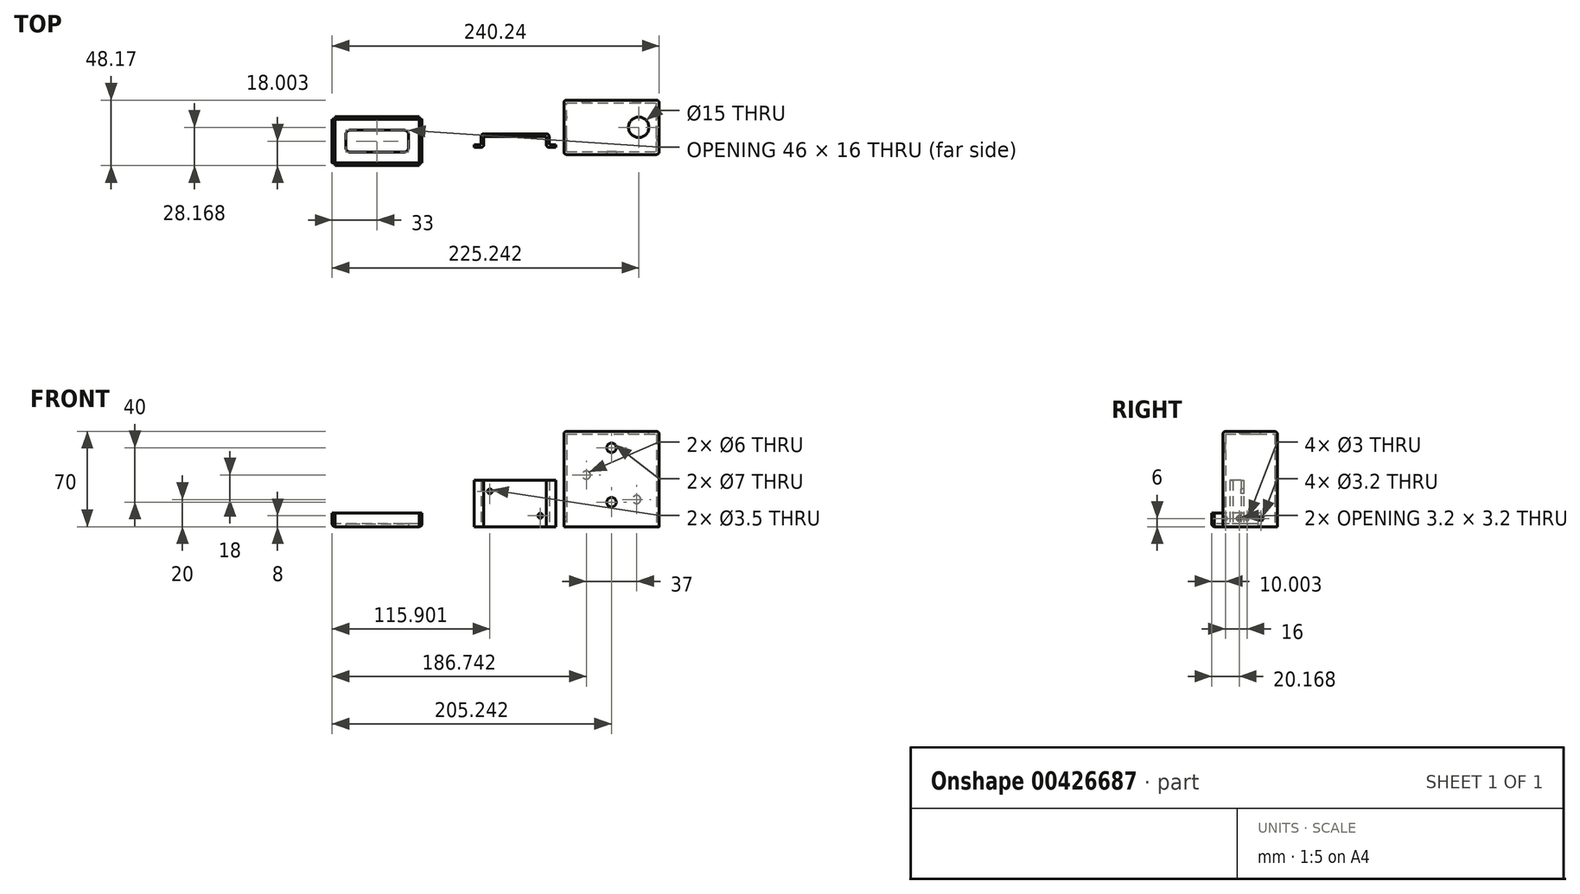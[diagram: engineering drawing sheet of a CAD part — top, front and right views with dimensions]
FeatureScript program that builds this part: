
annotation { "Feature Type Name" : "Feature", "Feature Type Description" : "" }
export const myFeature = defineFeature(function(context is Context, id is Id, definition is map)
    precondition{}
    {
        {
            var Q0;
            Q0=qCreatedBy(makeId("Top.planeOp"),FACE);
            var sketch = newSketch(context, id + "F0", { "sketchPlane" : qUnion([Q0])});
            skLineSegment(sketch, "E0", {"start": v(-40.1, 0) * mm, "end": v(-35.1, 0) * mm});
            skLineSegment(sketch, "E1", {"start": v(-40.1, 0) * mm, "end": v(-40.1, -2) * mm});
            skLineSegment(sketch, "E2", {"start": v(-35.1, 0) * mm, "end": v(-35.1, 6) * mm});
            skLineSegment(sketch, "E3", {"start": v(-33.1, 8) * mm, "end": v(12.9, 8) * mm});
            skLineSegment(sketch, "E4", {"start": v(14.9, 6) * mm, "end": v(14.9, 0) * mm});
            skLineSegment(sketch, "E5", {"start": v(14.9, 0) * mm, "end": v(19.9, 0) * mm});
            skLineSegment(sketch, "E6", {"start": v(19.9, 0) * mm, "end": v(19.9, -2) * mm});
            skLineSegment(sketch, "E7", {"start": v(19.9, -2) * mm, "end": v(14.9, -2) * mm});
            skLineSegment(sketch, "E8", {"start": v(12.9, 0) * mm, "end": v(12.9, 6) * mm});
            skLineSegment(sketch, "E9", {"start": v(12.9, 6) * mm, "end": v(-33.1, 6) * mm});
            skLineSegment(sketch, "E10", {"start": v(-33.1, 6) * mm, "end": v(-33.1, 0) * mm});
            skLineSegment(sketch, "E11", {"start": v(-35.1, -2) * mm, "end": v(-40.1, -2) * mm});
            skPoint(sketch, "E12.visualSharp", {"position": v(-35.1, 8) * mm});
            skArc(sketch, "E12.filletArc", {"start": v(-33.1, 8) * mm, "mid": v(-34.52, 7.41) * mm, "end": v(-35.1, 6) * mm});
            skPoint(sketch, "E13.visualSharp", {"position": v(-33.1, -2) * mm});
            skArc(sketch, "E13.filletArc", {"start": v(-35.1, -2) * mm, "mid": v(-33.7, -1.41) * mm, "end": v(-33.1, 0) * mm});
            skPoint(sketch, "E14.visualSharp", {"position": v(14.9, 8) * mm});
            skArc(sketch, "E14.filletArc", {"start": v(14.9, 6) * mm, "mid": v(14.3, 7.41) * mm, "end": v(12.9, 8) * mm});
            skPoint(sketch, "E15.visualSharp", {"position": v(12.9, -2) * mm});
            skArc(sketch, "E15.filletArc", {"start": v(12.9, 0) * mm, "mid": v(13.48, -1.41) * mm, "end": v(14.9, -2) * mm});
            skSolve(sketch);
        }
        {
            var Q0;
            Q0 = qSketchRegion(id + "F0", true);
            extrude(context, id + "F1", {"entities" : qUnion([Q0]), "depth" : 34 * mm});
        }
        {
            var Q0;
            Q0=makeQuery(id+"F1.opExtrude","SWEPT_FACE",FACE,{"disambiguationData":[OSD([sQuery(id+"F0.wireOp",EDGE,"E9")])]});
            var sketch = newSketch(context, id + "F2", { "sketchPlane" : qUnion([Q0])});
            skPoint(sketch, "E16", {"position": v(-28.6, 26) * mm});
            skPoint(sketch, "E17", {"position": v(8.4, 8) * mm});
            skSolve(sketch);
        }
        {
            var Q0;
            Q0=sQuery(id+"F2.wireOp",VERTEX,"E16");
            var Q1;
            Q1=sQuery(id+"F2.wireOp",VERTEX,"E17");
            var Q2;
            Q2=makeQuery(id+"F1.opExtrude","SWEPT_BODY",BODY,{"disambiguationData":[OSD([sQuery(id+"F0.wireOp",EDGE,"E0"),sQuery(id+"F0.wireOp",EDGE,"E1"),sQuery(id+"F0.wireOp",EDGE,"E2"),sQuery(id+"F0.wireOp",EDGE,"E3"),sQuery(id+"F0.wireOp",EDGE,"E4"),sQuery(id+"F0.wireOp",EDGE,"E5"),sQuery(id+"F0.wireOp",EDGE,"E6"),sQuery(id+"F0.wireOp",EDGE,"E7"),sQuery(id+"F0.wireOp",EDGE,"E8"),sQuery(id+"F0.wireOp",EDGE,"E9"),sQuery(id+"F0.wireOp",EDGE,"E10"),sQuery(id+"F0.wireOp",EDGE,"E11"),sQuery(id+"F0.wireOp",EDGE,"E12.filletArc"),sQuery(id+"F0.wireOp",EDGE,"E13.filletArc"),sQuery(id+"F0.wireOp",EDGE,"E14.filletArc"),sQuery(id+"F0.wireOp",EDGE,"E15.filletArc")])]});
            hole(context, id + "F3", {"style" : HoleStyle.SIMPLE, "endStyle" : HoleEndStyle.THROUGH, "holeDiameter" : 3.5 * mm, "tappedDepth" : 12 * mm, "tapClearance" : 3, "locations" : qUnion([Q0, Q1]), "scope" : qUnion([Q2])});
        }
        {
            var Q0;
            Q0=qCreatedBy(makeId("Top.planeOp"),FACE);
            var sketch = newSketch(context, id + "F4", { "sketchPlane" : qUnion([Q0])});
            skLineSegment(sketch, "E18.bottom", {"start": v(25.73, 32.75) * mm, "end": v(95.73, 32.75) * mm});
            skLineSegment(sketch, "E18.top", {"start": v(25.73, -7.25) * mm, "end": v(95.73, -7.25) * mm});
            skLineSegment(sketch, "E18.left", {"start": v(25.73, 32.75) * mm, "end": v(25.73, -7.25) * mm});
            skLineSegment(sketch, "E18.right", {"start": v(95.73, 32.75) * mm, "end": v(95.73, -7.25) * mm});
            skSolve(sketch);
        }
        {
            var Q0;
            Q0=makeQuery(id+"F4.imprint","IMPRINT",FACE,{"disambiguationData":[TD([[makeQuery(id+"F4.imprint","IMPRINT",EDGE,{"derivedFrom":sQuery(id+"F4.wireOp",EDGE,"E18.bottom")}),-1.0]])]});
            extrude(context, id + "F5", {"entities" : qUnion([Q0]), "depth" : 70 * mm});
        }
        {
            var Q0;
            Q0=makeQuery(id+"F5.opExtrude","CAP_FACE",FACE,{"disambiguationData":[OSD([sQuery(id+"F4.wireOp",EDGE,"E18.bottom"),sQuery(id+"F4.wireOp",EDGE,"E18.top"),sQuery(id+"F4.wireOp",EDGE,"E18.left"),sQuery(id+"F4.wireOp",EDGE,"E18.right")])],"isStart":true});
            var sketch = newSketch(context, id + "F6", { "sketchPlane" : qUnion([Q0])});
            skLineSegment(sketch, "E19.bottom", {"start": v(27.73, 5.25) * mm, "end": v(93.73, 5.25) * mm});
            skLineSegment(sketch, "E19.top", {"start": v(27.73, -30.75) * mm, "end": v(93.73, -30.75) * mm});
            skLineSegment(sketch, "E19.left", {"start": v(27.73, 5.25) * mm, "end": v(27.73, -30.75) * mm});
            skLineSegment(sketch, "E19.right", {"start": v(93.73, 5.25) * mm, "end": v(93.73, -30.75) * mm});
            skSolve(sketch);
        }
        {
            var Q0;
            Q0 = qSketchRegion(id + "F6", true);
            extrude(context, id + "F7", {"entities" : qUnion([Q0]), "operationType" : NewBodyOperationType.REMOVE, "oppositeDirection" : true, "depth" : 68 * mm});
        }
        {
            var Q0;
            Q0=makeQuery(id+"F5.opExtrude","CAP_FACE",FACE,{"disambiguationData":[OSD([sQuery(id+"F4.wireOp",EDGE,"E18.bottom"),sQuery(id+"F4.wireOp",EDGE,"E18.top"),sQuery(id+"F4.wireOp",EDGE,"E18.left"),sQuery(id+"F4.wireOp",EDGE,"E18.right")])],"isStart":false});
            var sketch = newSketch(context, id + "F8", { "sketchPlane" : qUnion([Q0])});
            skPoint(sketch, "E20", {"position": v(80.73, 12.75) * mm});
            skSolve(sketch);
        }
        {
            var Q0;
            Q0=sQuery(id+"F8.wireOp",VERTEX,"E20");
            var Q1;
            Q1=makeQuery(id+"F5.opExtrude","SWEPT_BODY",BODY,{"disambiguationData":[OSD([sQuery(id+"F4.wireOp",EDGE,"E18.bottom"),sQuery(id+"F4.wireOp",EDGE,"E18.top"),sQuery(id+"F4.wireOp",EDGE,"E18.left"),sQuery(id+"F4.wireOp",EDGE,"E18.right")])]});
            hole(context, id + "F9", {"style" : HoleStyle.SIMPLE, "endStyle" : HoleEndStyle.THROUGH, "holeDiameter" : 15 * mm, "tappedDepth" : 12 * mm, "tapClearance" : 3, "locations" : qUnion([Q0]), "scope" : qUnion([Q1])});
        }
        {
            var Q0;
            Q0=makeQuery(id+"F5.opExtrude","SWEPT_FACE",FACE,{"disambiguationData":[OSD([sQuery(id+"F4.wireOp",EDGE,"E18.right")])]});
            var sketch = newSketch(context, id + "F10", { "sketchPlane" : qUnion([Q0])});
            skPoint(sketch, "E21", {"position": v(4.75, 6) * mm});
            skPoint(sketch, "E22", {"position": v(20.75, 6) * mm});
            skSolve(sketch);
        }
        {
            var Q0;
            Q0=sQuery(id+"F10.wireOp",VERTEX,"E22");
            var Q1;
            Q1=sQuery(id+"F10.wireOp",VERTEX,"E21");
            var Q2;
            Q2=makeQuery(id+"F5.opExtrude","SWEPT_BODY",BODY,{"disambiguationData":[OSD([sQuery(id+"F4.wireOp",EDGE,"E18.bottom"),sQuery(id+"F4.wireOp",EDGE,"E18.top"),sQuery(id+"F4.wireOp",EDGE,"E18.left"),sQuery(id+"F4.wireOp",EDGE,"E18.right")])]});
            hole(context, id + "F11", {"style" : HoleStyle.SIMPLE, "endStyle" : HoleEndStyle.THROUGH, "holeDiameter" : 3.2 * mm, "tappedDepth" : 12 * mm, "tapClearance" : 3, "locations" : qUnion([Q0, Q1]), "scope" : qUnion([Q2])});
        }
        {
            var Q0;
            Q0=makeQuery(id+"F5.opExtrude","SWEPT_FACE",FACE,{"disambiguationData":[OSD([sQuery(id+"F4.wireOp",EDGE,"E18.bottom")])]});
            var sketch = newSketch(context, id + "F12", { "sketchPlane" : qUnion([Q0])});
            skCircle(sketch, "E23", {"center": v(-42.23, 38) * mm, "radius": 3 * mm});
            skCircle(sketch, "E24", {"center": v(-79.23, 20) * mm, "radius": 3 * mm});
            skSolve(sketch);
        }
        {
            var Q0;
            Q0=makeQuery(id+"F12.imprint","IMPRINT",FACE,{"disambiguationData":[TD([[makeQuery(id+"F12.imprint","IMPRINT",EDGE,{"derivedFrom":sQuery(id+"F12.wireOp",EDGE,"E23")}),1.0]])]});
            var Q1;
            Q1=makeQuery(id+"F12.imprint","IMPRINT",FACE,{"disambiguationData":[TD([[makeQuery(id+"F12.imprint","IMPRINT",EDGE,{"derivedFrom":sQuery(id+"F12.wireOp",EDGE,"E24")}),1.0]])]});
            extrude(context, id + "F13", {"entities" : qUnion([Q0, Q1]), "operationType" : NewBodyOperationType.REMOVE, "oppositeDirection" : true, "depth" : 2 * mm});
        }
        {
            var Q0;
            Q0=qCreatedBy(makeId("Top.planeOp"),FACE);
            var sketch = newSketch(context, id + "F14", { "sketchPlane" : qUnion([Q0])});
            skLineSegment(sketch, "E25.bottom", {"start": v(-142.5, 20.58) * mm, "end": v(-80.5, 20.58) * mm});
            skLineSegment(sketch, "E25.top", {"start": v(-142.5, -15.42) * mm, "end": v(-80.5, -15.42) * mm});
            skLineSegment(sketch, "E25.left", {"start": v(-144.5, 18.58) * mm, "end": v(-144.5, -13.42) * mm});
            skLineSegment(sketch, "E25.right", {"start": v(-78.5, 18.58) * mm, "end": v(-78.5, -13.42) * mm});
            skLineSegment(sketch, "E26", {"start": v(-142.5, 20.58) * mm, "end": v(-142.5, -15.42) * mm});
            skLineSegment(sketch, "E27", {"start": v(-144.5, 18.58) * mm, "end": v(-78.5, 18.58) * mm});
            skLineSegment(sketch, "E28", {"start": v(-80.5, 20.58) * mm, "end": v(-80.5, -15.42) * mm});
            skLineSegment(sketch, "E29", {"start": v(-144.5, -13.42) * mm, "end": v(-78.5, -13.42) * mm});
            skLineSegment(sketch, "E30.bottom", {"start": v(-131.5, 10.58) * mm, "end": v(-91.5, 10.58) * mm});
            skLineSegment(sketch, "E30.top", {"start": v(-131.5, -5.42) * mm, "end": v(-91.5, -5.42) * mm});
            skLineSegment(sketch, "E30.left", {"start": v(-134.5, 7.58) * mm, "end": v(-134.5, -2.42) * mm});
            skLineSegment(sketch, "E30.right", {"start": v(-88.5, 7.58) * mm, "end": v(-88.5, -2.42) * mm});
            skPoint(sketch, "E31.visualSharp", {"position": v(-134.5, 10.58) * mm});
            skArc(sketch, "E31.filletArc", {"start": v(-131.5, 10.58) * mm, "mid": v(-133.63, 9.7) * mm, "end": v(-134.5, 7.58) * mm});
            skPoint(sketch, "E32.visualSharp", {"position": v(-134.5, -5.42) * mm});
            skArc(sketch, "E32.filletArc", {"start": v(-134.5, -2.42) * mm, "mid": v(-133.63, -4.54) * mm, "end": v(-131.5, -5.42) * mm});
            skPoint(sketch, "E33.visualSharp", {"position": v(-88.5, -5.42) * mm});
            skArc(sketch, "E33.filletArc", {"start": v(-91.5, -5.42) * mm, "mid": v(-89.39, -4.54) * mm, "end": v(-88.5, -2.42) * mm});
            skPoint(sketch, "E34.visualSharp", {"position": v(-88.5, 10.58) * mm});
            skArc(sketch, "E34.filletArc", {"start": v(-88.5, 7.58) * mm, "mid": v(-89.39, 9.7) * mm, "end": v(-91.5, 10.58) * mm});
            skSolve(sketch);
        }
        {
            var Q0;
            Q0=makeQuery(id+"F14.imprint","IMPRINT",FACE,{"disambiguationData":[TD([[makeQuery(id+"F14.imprint","IMPRINT",EDGE,{"derivedFrom":sQuery(id+"F14.wireOp",EDGE,"E30.bottom")}),1.0]])]});
            var Q1;
            {var subQ0=sQuery(id+"F14.wireOp",EDGE,"E25.right");Q1=makeQuery(id+"F14.imprint","IMPRINT",FACE,{"disambiguationData":[TD([[makeQuery(id+"F14.imprint","IMPRINT",EDGE,{"derivedFrom":subQ0}),-1.0]])]});}
            var Q2;
            {var subQ0=sQuery(id+"F14.wireOp",EDGE,"E25.top");Q2=makeQuery(id+"F14.imprint","IMPRINT",FACE,{"disambiguationData":[TD([[makeQuery(id+"F14.imprint","IMPRINT",EDGE,{"derivedFrom":subQ0}),1.0]])]});}
            var Q3;
            {var subQ0=sQuery(id+"F14.wireOp",EDGE,"E25.left");Q3=makeQuery(id+"F14.imprint","IMPRINT",FACE,{"disambiguationData":[TD([[makeQuery(id+"F14.imprint","IMPRINT",EDGE,{"derivedFrom":subQ0}),1.0]])]});}
            var Q4;
            {var subQ0=sQuery(id+"F14.wireOp",EDGE,"E25.bottom");Q4=makeQuery(id+"F14.imprint","IMPRINT",FACE,{"disambiguationData":[TD([[makeQuery(id+"F14.imprint","IMPRINT",EDGE,{"derivedFrom":subQ0}),-1.0]])]});}
            extrude(context, id + "F15", {"entities" : qUnion([Q0, Q1, Q2, Q3, Q4]), "depth" : 2 * mm});
        }
        {
            var Q0;
            Q0=makeQuery(id+"F15.opExtrude","CAP_FACE",FACE,{"disambiguationData":[OSD([sQuery(id+"F14.wireOp",EDGE,"E25.bottom"),sQuery(id+"F14.wireOp",EDGE,"E25.top"),sQuery(id+"F14.wireOp",EDGE,"E25.left"),sQuery(id+"F14.wireOp",EDGE,"E25.right"),sQuery(id+"F14.wireOp",EDGE,"E26"),sQuery(id+"F14.wireOp",EDGE,"E27"),sQuery(id+"F14.wireOp",EDGE,"E28"),sQuery(id+"F14.wireOp",EDGE,"E29"),sQuery(id+"F14.wireOp",EDGE,"E30.bottom"),sQuery(id+"F14.wireOp",EDGE,"E30.top"),sQuery(id+"F14.wireOp",EDGE,"E30.left"),sQuery(id+"F14.wireOp",EDGE,"E30.right"),sQuery(id+"F14.wireOp",EDGE,"E31.filletArc"),sQuery(id+"F14.wireOp",EDGE,"E32.filletArc"),sQuery(id+"F14.wireOp",EDGE,"E33.filletArc"),sQuery(id+"F14.wireOp",EDGE,"E34.filletArc")])],"isStart":false});
            var sketch = newSketch(context, id + "F16", { "sketchPlane" : qUnion([Q0])});
            skLineSegment(sketch, "E35.bottom", {"start": v(-144.5, 18.58) * mm, "end": v(-142.6, 18.58) * mm});
            skLineSegment(sketch, "E35.top", {"start": v(-144.5, -13.42) * mm, "end": v(-142.6, -13.42) * mm});
            skLineSegment(sketch, "E35.left", {"start": v(-144.5, 18.58) * mm, "end": v(-144.5, -13.42) * mm});
            skLineSegment(sketch, "E35.right", {"start": v(-142.5, 18.48) * mm, "end": v(-142.5, -13.32) * mm});
            skLineSegment(sketch, "E36.bottom", {"start": v(-142.4, 18.58) * mm, "end": v(-80.6, 18.58) * mm});
            skLineSegment(sketch, "E36.top", {"start": v(-142.5, 20.58) * mm, "end": v(-80.5, 20.58) * mm});
            skLineSegment(sketch, "E36.left", {"start": v(-142.5, 18.68) * mm, "end": v(-142.5, 20.58) * mm});
            skLineSegment(sketch, "E36.right", {"start": v(-80.5, 18.68) * mm, "end": v(-80.5, 20.58) * mm});
            skLineSegment(sketch, "E37.bottom", {"start": v(-80.4, 18.58) * mm, "end": v(-78.5, 18.58) * mm});
            skLineSegment(sketch, "E37.top", {"start": v(-80.4, -13.42) * mm, "end": v(-78.5, -13.42) * mm});
            skLineSegment(sketch, "E37.left", {"start": v(-80.5, 18.48) * mm, "end": v(-80.5, -13.32) * mm});
            skLineSegment(sketch, "E37.right", {"start": v(-78.5, 18.58) * mm, "end": v(-78.5, -13.42) * mm});
            skLineSegment(sketch, "E38.bottom", {"start": v(-80.6, -13.42) * mm, "end": v(-142.4, -13.42) * mm});
            skLineSegment(sketch, "E38.top", {"start": v(-80.5, -15.42) * mm, "end": v(-142.5, -15.42) * mm});
            skLineSegment(sketch, "E38.left", {"start": v(-80.5, -13.52) * mm, "end": v(-80.5, -15.42) * mm});
            skLineSegment(sketch, "E38.right", {"start": v(-142.5, -13.52) * mm, "end": v(-142.5, -15.42) * mm});
            skPoint(sketch, "E39.visualSharp", {"position": v(-142.5, 18.58) * mm});
            skArc(sketch, "E39.filletArc", {"start": v(-142.5, 18.48) * mm, "mid": v(-142.54, 18.55) * mm, "end": v(-142.6, 18.58) * mm});
            skArc(sketch, "E40.filletArc", {"start": v(-142.5, 18.68) * mm, "mid": v(-142.48, 18.61) * mm, "end": v(-142.4, 18.58) * mm});
            skPoint(sketch, "E41.visualSharp", {"position": v(-80.5, 18.58) * mm});
            skArc(sketch, "E41.filletArc", {"start": v(-80.6, 18.58) * mm, "mid": v(-80.54, 18.61) * mm, "end": v(-80.5, 18.68) * mm});
            skArc(sketch, "E42.filletArc", {"start": v(-80.4, 18.58) * mm, "mid": v(-80.48, 18.55) * mm, "end": v(-80.5, 18.48) * mm});
            skPoint(sketch, "E43.visualSharp", {"position": v(-80.5, -13.42) * mm});
            skArc(sketch, "E43.filletArc", {"start": v(-80.5, -13.32) * mm, "mid": v(-80.48, -13.39) * mm, "end": v(-80.4, -13.42) * mm});
            skArc(sketch, "E44.filletArc", {"start": v(-80.5, -13.52) * mm, "mid": v(-80.54, -13.45) * mm, "end": v(-80.6, -13.42) * mm});
            skPoint(sketch, "E45.visualSharp", {"position": v(-142.5, -13.42) * mm});
            skArc(sketch, "E45.filletArc", {"start": v(-142.4, -13.42) * mm, "mid": v(-142.48, -13.45) * mm, "end": v(-142.5, -13.52) * mm});
            skArc(sketch, "E46.filletArc", {"start": v(-142.6, -13.42) * mm, "mid": v(-142.54, -13.39) * mm, "end": v(-142.5, -13.32) * mm});
            skSolve(sketch);
        }
        {
            var Q0;
            Q0=makeQuery(id+"F16.imprint","IMPRINT",FACE,{"disambiguationData":[TD([[makeQuery(id+"F16.imprint","IMPRINT",EDGE,{"derivedFrom":sQuery(id+"F16.wireOp",EDGE,"E36.bottom")}),1.0]])]});
            var Q1;
            Q1=makeQuery(id+"F16.imprint","IMPRINT",FACE,{"disambiguationData":[TD([[makeQuery(id+"F16.imprint","IMPRINT",EDGE,{"derivedFrom":sQuery(id+"F16.wireOp",EDGE,"E35.bottom")}),-1.0]])]});
            var Q2;
            Q2=makeQuery(id+"F16.imprint","IMPRINT",FACE,{"disambiguationData":[TD([[makeQuery(id+"F16.imprint","IMPRINT",EDGE,{"derivedFrom":sQuery(id+"F16.wireOp",EDGE,"E38.bottom")}),1.0]])]});
            var Q3;
            Q3=makeQuery(id+"F16.imprint","IMPRINT",FACE,{"disambiguationData":[TD([[makeQuery(id+"F16.imprint","IMPRINT",EDGE,{"derivedFrom":sQuery(id+"F16.wireOp",EDGE,"E37.bottom")}),-1.0]])]});
            extrude(context, id + "F17", {"entities" : qUnion([Q0, Q1, Q2, Q3]), "operationType" : NewBodyOperationType.ADD, "depth" : 8 * mm});
        }
        {
            var Q0;
            Q0=makeQuery(id+"F17.boolean.opBoolean","MERGE",FACE,{"derivedFrom":[makeQuery(id+"F15.opExtrude","SWEPT_FACE",FACE,{"disambiguationData":[OSD([sQuery(id+"F14.wireOp",EDGE,"E25.left")])]}),makeQuery(id+"F17.opExtrude","SWEPT_FACE",FACE,{"disambiguationData":[OSD([sQuery(id+"F16.wireOp",EDGE,"E35.left")])]})]});
            var sketch = newSketch(context, id + "F18", { "sketchPlane" : qUnion([Q0])});
            skPoint(sketch, "E47", {"position": v(-10.58, 6) * mm});
            skPoint(sketch, "E48", {"position": v(5.42, 6) * mm});
            skSolve(sketch);
        }
        {
            var Q0;
            Q0=sQuery(id+"F18.wireOp",VERTEX,"E47");
            var Q1;
            Q1=sQuery(id+"F18.wireOp",VERTEX,"E48");
            var Q2;
            Q2=makeQuery(id+"F15.opExtrude","SWEPT_BODY",BODY,{"disambiguationData":[OSD([sQuery(id+"F14.wireOp",EDGE,"E25.bottom"),sQuery(id+"F14.wireOp",EDGE,"E25.top"),sQuery(id+"F14.wireOp",EDGE,"E25.left"),sQuery(id+"F14.wireOp",EDGE,"E25.right"),sQuery(id+"F14.wireOp",EDGE,"E26"),sQuery(id+"F14.wireOp",EDGE,"E27"),sQuery(id+"F14.wireOp",EDGE,"E28"),sQuery(id+"F14.wireOp",EDGE,"E29"),sQuery(id+"F14.wireOp",EDGE,"E30.bottom"),sQuery(id+"F14.wireOp",EDGE,"E30.top"),sQuery(id+"F14.wireOp",EDGE,"E30.left"),sQuery(id+"F14.wireOp",EDGE,"E30.right"),sQuery(id+"F14.wireOp",EDGE,"E31.filletArc"),sQuery(id+"F14.wireOp",EDGE,"E32.filletArc"),sQuery(id+"F14.wireOp",EDGE,"E33.filletArc"),sQuery(id+"F14.wireOp",EDGE,"E34.filletArc")])]});
            hole(context, id + "F19", {"style" : HoleStyle.SIMPLE, "endStyle" : HoleEndStyle.THROUGH, "holeDiameter" : 3 * mm, "tappedDepth" : 12 * mm, "tapClearance" : 3, "locations" : qUnion([Q0, Q1]), "scope" : qUnion([Q2])});
        }
        {
            var Q0;
            Q0=makeQuery(id+"F15.opExtrude","CAP_EDGE",EDGE,{"disambiguationData":[OSD([sQuery(id+"F14.wireOp",EDGE,"E25.left")])],"isStart":true});
            var Q1;
            Q1=makeQuery(id+"F15.opExtrude","CAP_EDGE",EDGE,{"disambiguationData":[OSD([sQuery(id+"F14.wireOp",EDGE,"E25.bottom")])],"isStart":true});
            var Q2;
            Q2=makeQuery(id+"F15.opExtrude","CAP_EDGE",EDGE,{"disambiguationData":[OSD([sQuery(id+"F14.wireOp",EDGE,"E25.right")])],"isStart":true});
            var Q3;
            Q3=makeQuery(id+"F15.opExtrude","CAP_EDGE",EDGE,{"disambiguationData":[OSD([sQuery(id+"F14.wireOp",EDGE,"E25.top")])],"isStart":true});
            fillet(context, id + "F20", {"entities" : qUnion([Q0, Q1, Q2, Q3]), "radius" : 2 * mm, "tangentPropagation" : true, "allowEdgeOverflow" : false});
        }
        {
            var Q0;
            Q0=makeQuery(id+"F5.opExtrude","SWEPT_EDGE",EDGE,{"disambiguationData":[OSD([sQuery(id+"F4.wireOp",EDGE,"E18.bottom"),sQuery(id+"F4.wireOp",EDGE,"E18.right")])]});
            var Q1;
            Q1=makeQuery(id+"F5.opExtrude","CAP_EDGE",EDGE,{"disambiguationData":[OSD([sQuery(id+"F4.wireOp",EDGE,"E18.bottom")])],"isStart":false});
            var Q2;
            Q2=makeQuery(id+"F5.opExtrude","CAP_EDGE",EDGE,{"disambiguationData":[OSD([sQuery(id+"F4.wireOp",EDGE,"E18.right")])],"isStart":false});
            var Q3;
            Q3=makeQuery(id+"F5.opExtrude","SWEPT_EDGE",EDGE,{"disambiguationData":[OSD([sQuery(id+"F4.wireOp",EDGE,"E18.top"),sQuery(id+"F4.wireOp",EDGE,"E18.right")])]});
            var Q4;
            Q4=makeQuery(id+"F5.opExtrude","CAP_EDGE",EDGE,{"disambiguationData":[OSD([sQuery(id+"F4.wireOp",EDGE,"E18.left")])],"isStart":false});
            var Q5;
            Q5=makeQuery(id+"F5.opExtrude","CAP_EDGE",EDGE,{"disambiguationData":[OSD([sQuery(id+"F4.wireOp",EDGE,"E18.top")])],"isStart":false});
            var Q6;
            Q6=makeQuery(id+"F5.opExtrude","SWEPT_EDGE",EDGE,{"disambiguationData":[OSD([sQuery(id+"F4.wireOp",EDGE,"E18.bottom"),sQuery(id+"F4.wireOp",EDGE,"E18.left")])]});
            var Q7;
            Q7=makeQuery(id+"F5.opExtrude","SWEPT_EDGE",EDGE,{"disambiguationData":[OSD([sQuery(id+"F4.wireOp",EDGE,"E18.top"),sQuery(id+"F4.wireOp",EDGE,"E18.left")])]});
            fillet(context, id + "F21", {"entities" : qUnion([Q0, Q1, Q2, Q3, Q4, Q5, Q6, Q7]), "radius" : 2 * mm, "tangentPropagation" : true, "allowEdgeOverflow" : false});
        }
        {
            var Q0;
            Q0=makeQuery(id+"F5.opExtrude","SWEPT_FACE",FACE,{"disambiguationData":[OSD([sQuery(id+"F4.wireOp",EDGE,"E18.top")])]});
            var sketch = newSketch(context, id + "F22", { "sketchPlane" : qUnion([Q0])});
            skCircle(sketch, "E49", {"center": v(60.73, 58) * mm, "radius": 3.5 * mm});
            skCircle(sketch, "E50", {"center": v(60.73, 18) * mm, "radius": 3.5 * mm});
            skSolve(sketch);
        }
        {
            var Q0;
            Q0=makeQuery(id+"F22.imprint","IMPRINT",FACE,{"disambiguationData":[TD([[makeQuery(id+"F22.imprint","IMPRINT",EDGE,{"derivedFrom":sQuery(id+"F22.wireOp",EDGE,"E49")}),1.0]])]});
            var Q1;
            Q1=makeQuery(id+"F22.imprint","IMPRINT",FACE,{"disambiguationData":[TD([[makeQuery(id+"F22.imprint","IMPRINT",EDGE,{"derivedFrom":sQuery(id+"F22.wireOp",EDGE,"E50")}),1.0]])]});
            extrude(context, id + "F23", {"entities" : qUnion([Q0, Q1]), "operationType" : NewBodyOperationType.REMOVE, "oppositeDirection" : true, "depth" : 2 * mm});
        }
    });
